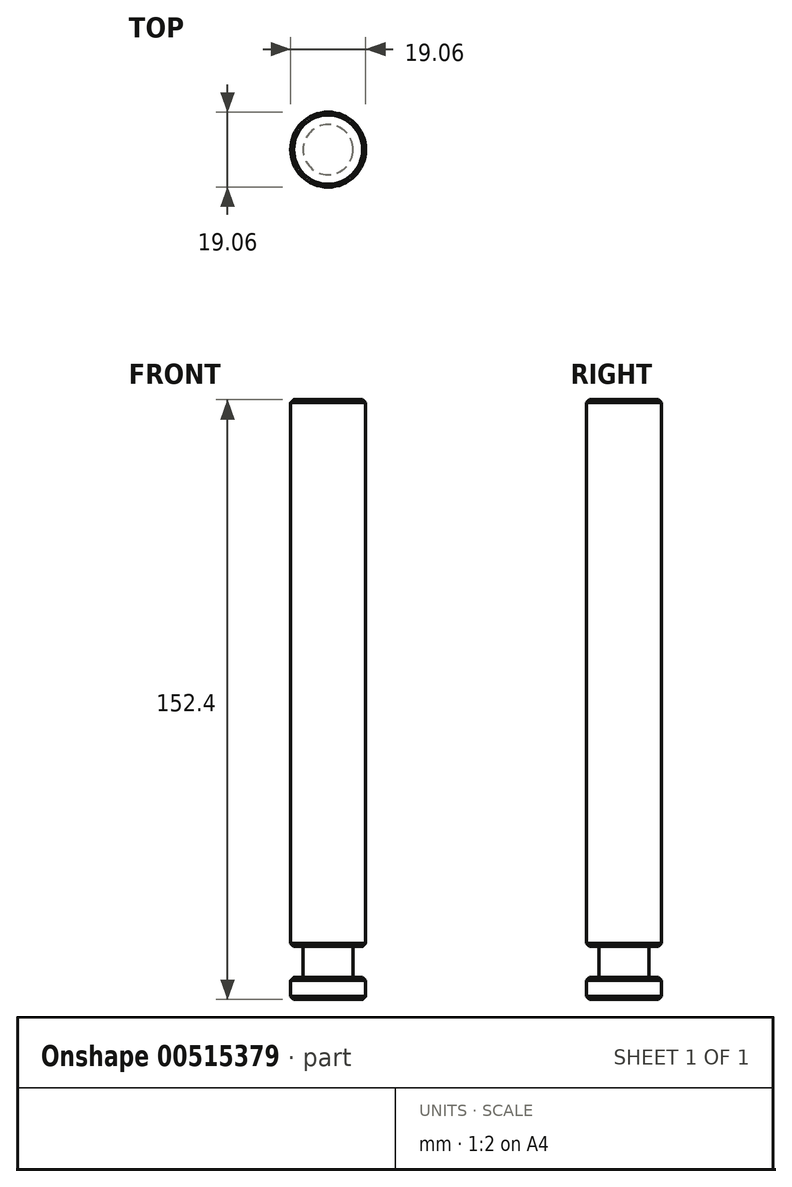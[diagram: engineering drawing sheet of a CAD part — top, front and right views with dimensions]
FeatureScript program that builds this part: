
annotation { "Feature Type Name" : "Feature", "Feature Type Description" : "" }
export const myFeature = defineFeature(function(context is Context, id is Id, definition is map)
    precondition{}
    {
        {
            var Q0;
            Q0=qCreatedBy(makeId("Right.planeOp"),FACE);
            var sketch = newSketch(context, id + "F0", { "sketchPlane" : qUnion([Q0])});
            skLineSegment(sketch, "E0", {"start": v(0, 0) * mm, "end": v(9.53, 0) * mm});
            skLineSegment(sketch, "E1", {"start": v(9.53, 0) * mm, "end": v(9.53, 5.56) * mm});
            skLineSegment(sketch, "E2", {"start": v(9.53, 5.56) * mm, "end": v(6.35, 5.56) * mm});
            skLineSegment(sketch, "E3", {"start": v(6.35, 5.56) * mm, "end": v(6.35, 13.5) * mm});
            skLineSegment(sketch, "E4", {"start": v(6.35, 13.5) * mm, "end": v(9.53, 13.5) * mm});
            skLineSegment(sketch, "E5", {"start": v(9.53, 13.5) * mm, "end": v(9.53, 152.4) * mm});
            skLineSegment(sketch, "E6", {"start": v(9.53, 152.4) * mm, "end": v(0, 152.4) * mm});
            skLineSegment(sketch, "E7", {"start": v(0, 152.4) * mm, "end": v(0, 0) * mm});
            skSolve(sketch);
        }
        {
            var Q0;
            Q0=makeQuery(id+"F0.imprint","IMPRINT",FACE,{"disambiguationData":[TD([[makeQuery(id+"F0.imprint","IMPRINT",EDGE,{"derivedFrom":sQuery(id+"F0.wireOp",EDGE,"E0")}),1.0]])]});
            var Q1;
            Q1=sQuery(id+"F0.wireOp",EDGE,"E7");
            revolve(context, id + "F1", {"entities" : qUnion([Q0]), "axis" : qUnion([Q1]), "revolveType" : RevolveType.FULL});
        }
        {
            var Q0;
            Q0=makeQuery(id+"F1.opRevolve","SWEPT_EDGE",EDGE,{"disambiguationData":[OSD([sQuery(id+"F0.wireOp",EDGE,"E5"),sQuery(id+"F0.wireOp",EDGE,"E6")])]});
            var Q1;
            Q1=makeQuery(id+"F1.opRevolve","SWEPT_EDGE",EDGE,{"disambiguationData":[OSD([sQuery(id+"F0.wireOp",EDGE,"E1"),sQuery(id+"F0.wireOp",EDGE,"E2")])]});
            var Q2;
            Q2=makeQuery(id+"F1.opRevolve","SWEPT_EDGE",EDGE,{"disambiguationData":[OSD([sQuery(id+"F0.wireOp",EDGE,"E4"),sQuery(id+"F0.wireOp",EDGE,"E5")])]});
            var Q3;
            Q3=makeQuery(id+"F1.opRevolve","SWEPT_EDGE",EDGE,{"disambiguationData":[OSD([sQuery(id+"F0.wireOp",EDGE,"E0"),sQuery(id+"F0.wireOp",EDGE,"E1")])]});
            chamfer(context, id + "F2", {"entities" : qUnion([Q0, Q1, Q2, Q3]), "width" : 0.76 * mm, "tangentPropagation" : true});
        }
    });
